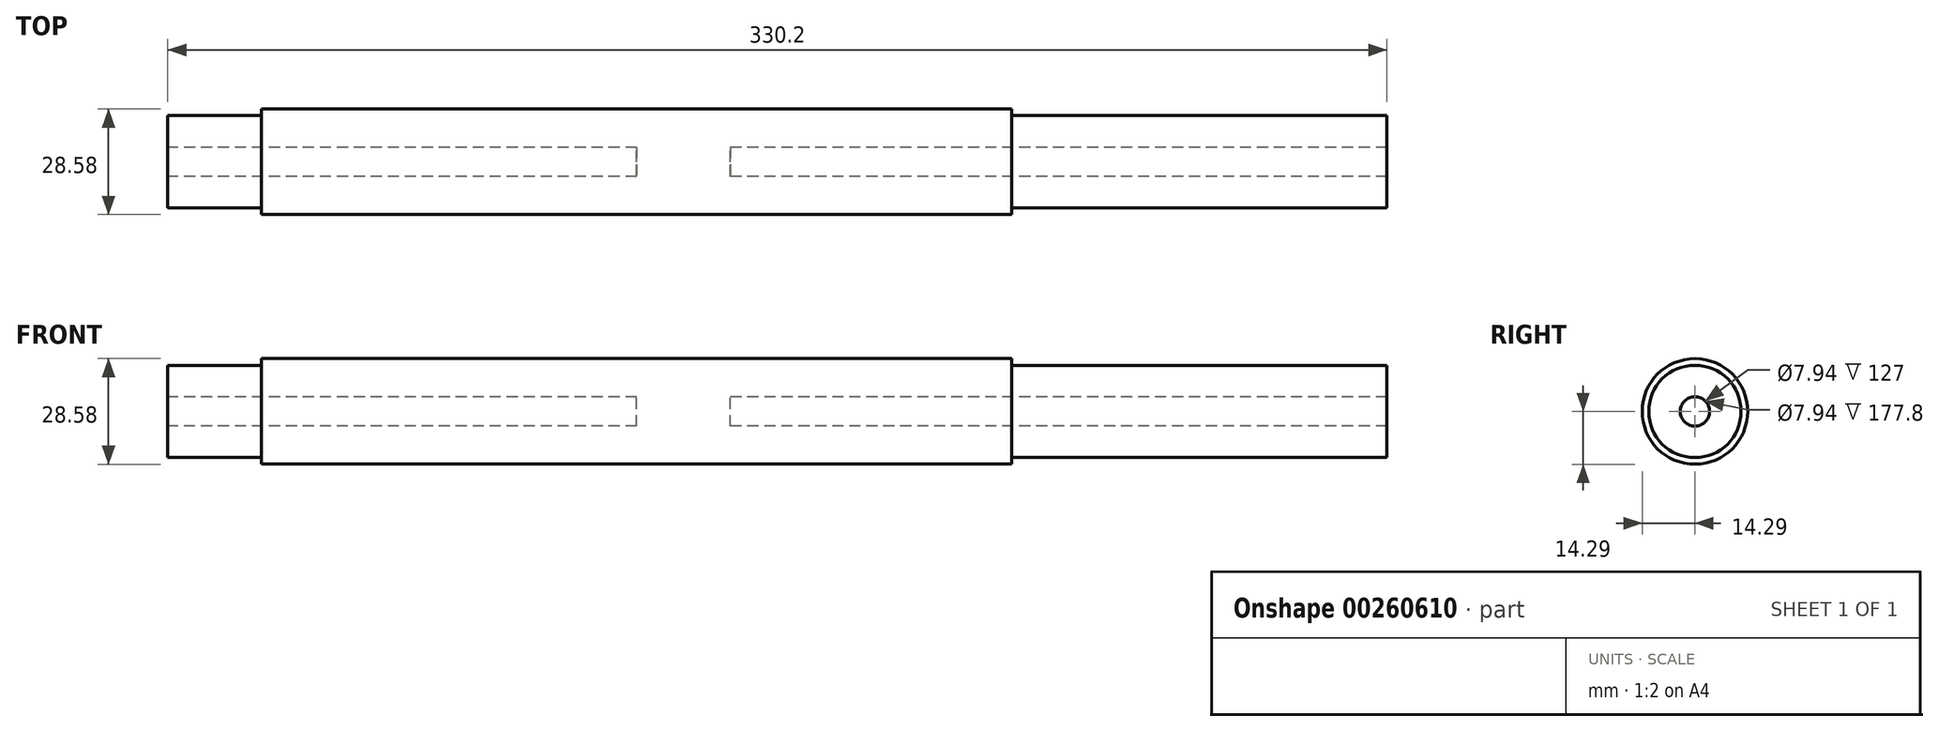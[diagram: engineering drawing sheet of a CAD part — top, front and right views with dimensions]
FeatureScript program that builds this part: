
annotation { "Feature Type Name" : "Feature", "Feature Type Description" : "" }
export const myFeature = defineFeature(function(context is Context, id is Id, definition is map)
    precondition{}
    {
        {
            var Q0;
            Q0=qCreatedBy(makeId("Right.planeOp"),FACE);
            var sketch = newSketch(context, id + "F0", { "sketchPlane" : qUnion([Q0])});
            skCircle(sketch, "E0", {"center": v(0, 0) * mm, "radius": 12.5 * mm});
            skCircle(sketch, "E1", {"center": v(0, 0) * mm, "radius": 14.29 * mm});
            skCircle(sketch, "E2", {"center": v(0, 0) * mm, "radius": 3.97 * mm});
            skSolve(sketch);
        }
        {
            var Q0;
            Q0=makeQuery(id+"F0.imprint","IMPRINT",FACE,{"disambiguationData":[TD([[makeQuery(id+"F0.imprint","IMPRINT",EDGE,{"derivedFrom":sQuery(id+"F0.wireOp",EDGE,"E0")}),-1.0]])]});
            extrude(context, id + "F1", {"entities" : qUnion([Q0]), "depth" : 101.6 * mm, "hasSecondDirection" : true, "secondDirectionOppositeDirection" : true, "secondDirectionDepth" : 101.6 * mm});
        }
        {
            var Q0;
            Q0=makeQuery(id+"F0.imprint","IMPRINT",FACE,{"disambiguationData":[TD([[makeQuery(id+"F0.imprint","IMPRINT",EDGE,{"derivedFrom":sQuery(id+"F0.wireOp",EDGE,"E0")}),1.0]])]});
            extrude(context, id + "F2", {"entities" : qUnion([Q0]), "operationType" : NewBodyOperationType.ADD, "depth" : 203.2 * mm, "hasSecondDirection" : true, "secondDirectionOppositeDirection" : true, "secondDirectionDepth" : 127 * mm});
        }
        {
            var Q0;
            Q0=makeQuery(id+"F0.imprint","IMPRINT",FACE,{"disambiguationData":[TD([[makeQuery(id+"F0.imprint","IMPRINT",EDGE,{"derivedFrom":sQuery(id+"F0.wireOp",EDGE,"E2")}),1.0]])]});
            extrude(context, id + "F3", {"entities" : qUnion([Q0]), "operationType" : NewBodyOperationType.ADD, "depth" : 25.4 * mm});
        }
    });
